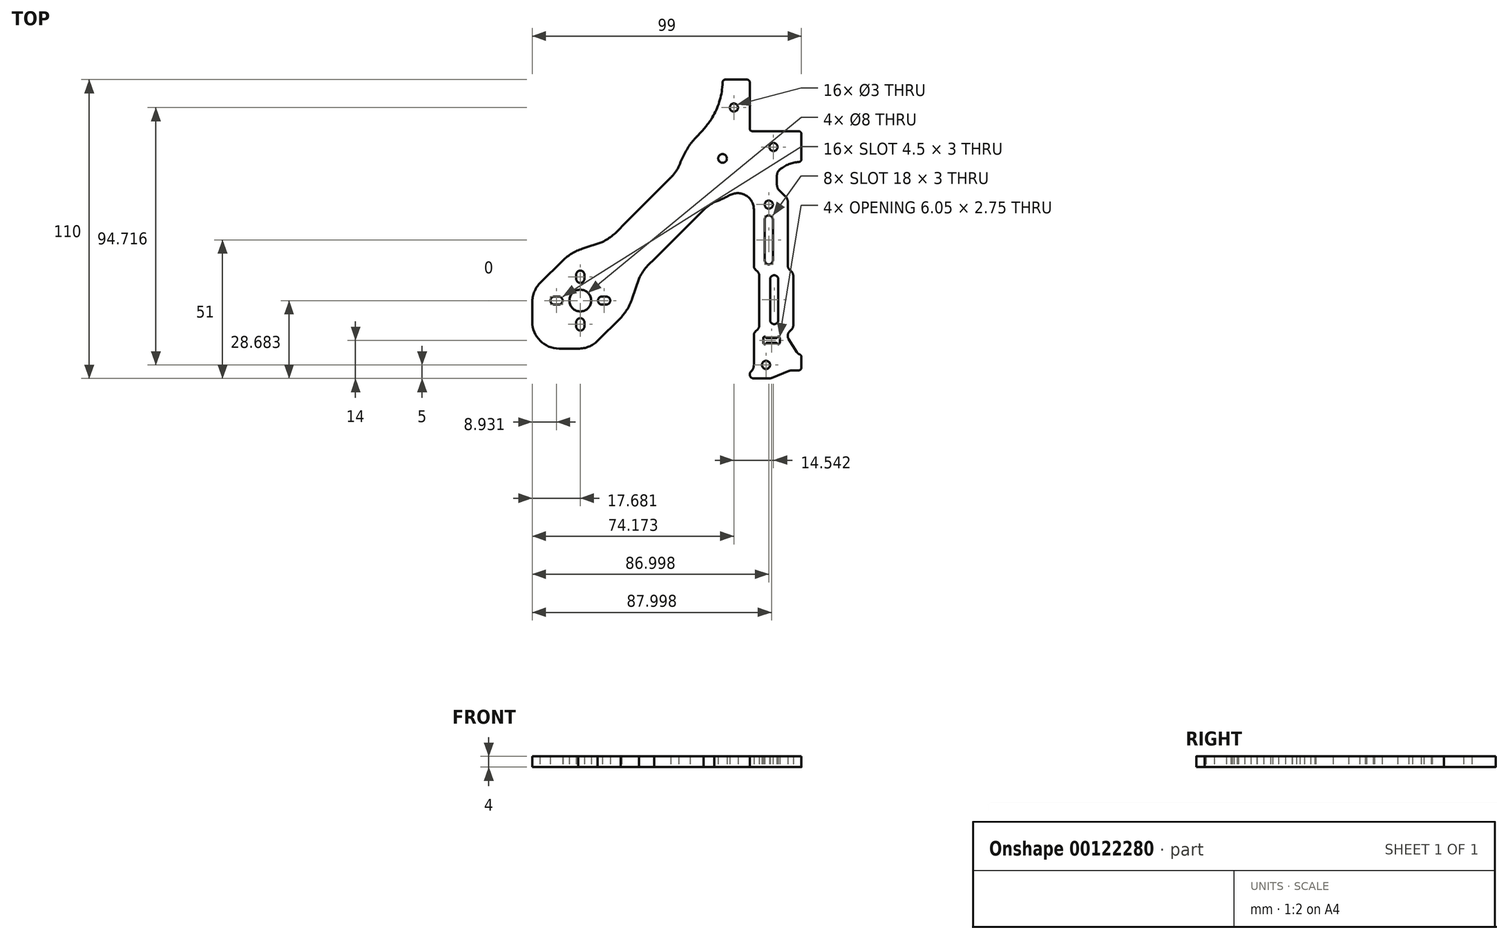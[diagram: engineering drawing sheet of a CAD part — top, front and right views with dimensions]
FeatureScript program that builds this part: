
annotation { "Feature Type Name" : "Feature", "Feature Type Description" : "" }
export const myFeature = defineFeature(function(context is Context, id is Id, definition is map)
    precondition{}
    {
        {
            var Q0;
            Q0=qCreatedBy(makeId("Top.planeOp"),FACE);
            var sketch = newSketch(context, id + "F0", { "sketchPlane" : qUnion([Q0])});
            skLineSegment(sketch, "E0", {"start": v(32, -55) * mm, "end": v(37.42, -55) * mm});
            skArc(sketch, "E1", {"start": v(31, -52.38) * mm, "mid": v(30.6, -54.04) * mm, "end": v(32, -55) * mm});
            skLineSegment(sketch, "E2", {"start": v(44.96, -52.21) * mm, "end": v(38.53, -54.79) * mm});
            skArc(sketch, "E3", {"start": v(31, -52.38) * mm, "mid": v(31.74, -51.37) * mm, "end": v(32, -50.15) * mm});
            skArc(sketch, "E4", {"start": v(37.42, -55) * mm, "mid": v(37.99, -54.95) * mm, "end": v(38.53, -54.79) * mm});
            skArc(sketch, "E5", {"start": v(46.08, -52) * mm, "mid": v(45.5, -52.05) * mm, "end": v(44.96, -52.21) * mm});
            skCircle(sketch, "E6", {"center": v(37.5, 9) * mm, "radius": 1.5 * mm});
            skLineSegment(sketch, "E7", {"start": v(46.08, -52) * mm, "end": v(48.5, -52) * mm});
            skArc(sketch, "E8", {"start": v(48.5, -52) * mm, "mid": v(49.2, -51.7) * mm, "end": v(49.5, -51) * mm});
            skLineSegment(sketch, "E9", {"start": v(33.41, -15.73) * mm, "end": v(32.58, -14.9) * mm});
            skLineSegment(sketch, "E10", {"start": v(32.58, -37.73) * mm, "end": v(33.41, -36.9) * mm});
            skLineSegment(sketch, "E11", {"start": v(32, -39.15) * mm, "end": v(32, -50.15) * mm});
            skLineSegment(sketch, "E12", {"start": v(34, -17.15) * mm, "end": v(34, -35.49) * mm});
            skArc(sketch, "E13", {"start": v(32.58, -37.73) * mm, "mid": v(32.15, -38.38) * mm, "end": v(32, -39.15) * mm});
            skArc(sketch, "E14", {"start": v(33.41, -36.9) * mm, "mid": v(33.85, -36.25) * mm, "end": v(34, -35.49) * mm});
            skArc(sketch, "E15", {"start": v(32, -13.49) * mm, "mid": v(32.15, -14.25) * mm, "end": v(32.58, -14.9) * mm});
            skArc(sketch, "E16", {"start": v(34, -17.15) * mm, "mid": v(33.85, -16.38) * mm, "end": v(33.41, -15.73) * mm});
            skCircle(sketch, "E17", {"center": v(-31.82, -26.32) * mm, "radius": 4 * mm});
            skArc(sketch, "E18", {"start": v(-41.32, -24.82) * mm, "mid": v(-42.82, -26.32) * mm, "end": v(-41.32, -27.82) * mm});
            skArc(sketch, "E19", {"start": v(-39.82, -27.82) * mm, "mid": v(-38.32, -26.32) * mm, "end": v(-39.82, -24.82) * mm});
            skArc(sketch, "E20", {"start": v(-30.32, -16.82) * mm, "mid": v(-31.82, -15.32) * mm, "end": v(-33.32, -16.82) * mm});
            skArc(sketch, "E21", {"start": v(-33.32, -18.32) * mm, "mid": v(-31.82, -19.82) * mm, "end": v(-30.32, -18.32) * mm});
            skArc(sketch, "E22", {"start": v(-23.82, -24.82) * mm, "mid": v(-25.32, -26.32) * mm, "end": v(-23.82, -27.82) * mm});
            skArc(sketch, "E23", {"start": v(-22.32, -27.82) * mm, "mid": v(-20.82, -26.32) * mm, "end": v(-22.32, -24.82) * mm});
            skArc(sketch, "E24", {"start": v(-30.32, -34.32) * mm, "mid": v(-31.82, -32.82) * mm, "end": v(-33.32, -34.32) * mm});
            skArc(sketch, "E25", {"start": v(-33.32, -35.82) * mm, "mid": v(-31.82, -37.32) * mm, "end": v(-30.32, -35.82) * mm});
            skLineSegment(sketch, "E26", {"start": v(-41.32, -24.82) * mm, "end": v(-39.82, -24.82) * mm});
            skLineSegment(sketch, "E27", {"start": v(-39.82, -27.82) * mm, "end": v(-41.32, -27.82) * mm});
            skLineSegment(sketch, "E28", {"start": v(-33.32, -16.82) * mm, "end": v(-33.32, -18.32) * mm});
            skLineSegment(sketch, "E29", {"start": v(-30.32, -16.82) * mm, "end": v(-30.32, -18.32) * mm});
            skLineSegment(sketch, "E30", {"start": v(-22.32, -24.82) * mm, "end": v(-23.82, -24.82) * mm});
            skLineSegment(sketch, "E31", {"start": v(-22.32, -27.82) * mm, "end": v(-23.82, -27.82) * mm});
            skLineSegment(sketch, "E32", {"start": v(-30.32, -34.32) * mm, "end": v(-30.32, -35.82) * mm});
            skLineSegment(sketch, "E33", {"start": v(-33.32, -34.32) * mm, "end": v(-33.32, -35.82) * mm});
            skLineSegment(sketch, "E34", {"start": v(-25.46, -41.17) * mm, "end": v(-16.97, -32.68) * mm});
            skLineSegment(sketch, "E35", {"start": v(-38.18, -11.47) * mm, "end": v(-46.67, -19.95) * mm});
            skArc(sketch, "E36", {"start": v(-49.5, -34.1) * mm, "mid": v(-46.6, -41.1) * mm, "end": v(-39.6, -44) * mm});
            skLineSegment(sketch, "E37", {"start": v(-49.5, -34.1) * mm, "end": v(-49.5, -27.02) * mm});
            skLineSegment(sketch, "E38", {"start": v(-39.6, -44) * mm, "end": v(-32.53, -44) * mm});
            skLineSegment(sketch, "E39", {"start": v(-12.73, -25.61) * mm, "end": v(-10.25, -18.19) * mm});
            skLineSegment(sketch, "E40", {"start": v(-31.11, -7.23) * mm, "end": v(-23.69, -4.75) * mm});
            skArc(sketch, "E41", {"start": v(-23.69, -4.75) * mm, "mid": v(-19.85, -2.3) * mm, "end": v(-16.62, 0.9) * mm});
            skArc(sketch, "E42", {"start": v(-4.6, -11.11) * mm, "mid": v(-7.8, -14.35) * mm, "end": v(-10.25, -18.19) * mm});
            skArc(sketch, "E43", {"start": v(-16.97, -32.68) * mm, "mid": v(-14.48, -29.37) * mm, "end": v(-12.73, -25.61) * mm});
            skArc(sketch, "E44", {"start": v(-31.11, -7.23) * mm, "mid": v(-34.87, -8.98) * mm, "end": v(-38.18, -11.47) * mm});
            skArc(sketch, "E45", {"start": v(-46.67, -19.95) * mm, "mid": v(-48.79, -23.2) * mm, "end": v(-49.5, -27.02) * mm});
            skArc(sketch, "E46", {"start": v(-32.53, -44) * mm, "mid": v(-28.7, -43.28) * mm, "end": v(-25.46, -41.17) * mm});
            skLineSegment(sketch, "E47", {"start": v(1.41, 18.94) * mm, "end": v(-16.62, 0.9) * mm});
            skLineSegment(sketch, "E48", {"start": v(32, 7.22) * mm, "end": v(32, -13.49) * mm});
            skArc(sketch, "E49", {"start": v(17.5, 9.92) * mm, "mid": v(15.37, 8.64) * mm, "end": v(13.5, 7) * mm});
            skArc(sketch, "E50", {"start": v(1.41, 18.94) * mm, "mid": v(3.1, 20.84) * mm, "end": v(4.42, 23) * mm});
            skLineSegment(sketch, "E51", {"start": v(46.5, -17.15) * mm, "end": v(46.5, -35.49) * mm});
            skLineSegment(sketch, "E52", {"start": v(45.08, -37.73) * mm, "end": v(45.91, -36.9) * mm});
            skLineSegment(sketch, "E53", {"start": v(45.91, -15.73) * mm, "end": v(45.08, -14.9) * mm});
            skLineSegment(sketch, "E54", {"start": v(44.5, -13.49) * mm, "end": v(44.5, 9.96) * mm});
            skLineSegment(sketch, "E55", {"start": v(44.5, -39.43) * mm, "end": v(44.5, -39.15) * mm});
            skArc(sketch, "E56", {"start": v(44.5, -13.49) * mm, "mid": v(44.65, -14.25) * mm, "end": v(45.08, -14.9) * mm});
            skArc(sketch, "E57", {"start": v(46.5, -17.15) * mm, "mid": v(46.35, -16.38) * mm, "end": v(45.91, -15.73) * mm});
            skArc(sketch, "E58", {"start": v(45.08, -37.73) * mm, "mid": v(44.65, -38.38) * mm, "end": v(44.5, -39.15) * mm});
            skArc(sketch, "E59", {"start": v(45.91, -36.9) * mm, "mid": v(46.35, -36.25) * mm, "end": v(46.5, -35.49) * mm});
            skLineSegment(sketch, "E60", {"start": v(41, -33.5) * mm, "end": v(41, -18.5) * mm});
            skLineSegment(sketch, "E61", {"start": v(38, -18.5) * mm, "end": v(38, -33.5) * mm});
            skArc(sketch, "E62", {"start": v(38, -33.5) * mm, "mid": v(39.5, -35) * mm, "end": v(41, -33.5) * mm});
            skArc(sketch, "E63", {"start": v(41, -18.5) * mm, "mid": v(39.5, -17) * mm, "end": v(38, -18.5) * mm});
            skLineSegment(sketch, "E64", {"start": v(39, -11.5) * mm, "end": v(39, 3.5) * mm});
            skLineSegment(sketch, "E65", {"start": v(36, 3.5) * mm, "end": v(36, -11.5) * mm});
            skArc(sketch, "E66", {"start": v(36, -11.5) * mm, "mid": v(37.5, -13) * mm, "end": v(39, -11.5) * mm});
            skArc(sketch, "E67", {"start": v(39, 3.5) * mm, "mid": v(37.5, 5) * mm, "end": v(36, 3.5) * mm});
            skCircle(sketch, "E68", {"center": v(39.22, 30.17) * mm, "radius": 1.5 * mm});
            skCircle(sketch, "E69", {"center": v(24.67, 44.72) * mm, "radius": 1.5 * mm});
            skLineSegment(sketch, "E70", {"start": v(44.8, -40.49) * mm, "end": v(47.8, -45.29) * mm});
            skArc(sketch, "E71", {"start": v(44.5, -39.43) * mm, "mid": v(44.58, -39.98) * mm, "end": v(44.8, -40.49) * mm});
            skLineSegment(sketch, "E72", {"start": v(49.5, -47.05) * mm, "end": v(49.5, -51) * mm});
            skArc(sketch, "E73", {"start": v(47.8, -45.29) * mm, "mid": v(48.25, -45.79) * mm, "end": v(48.83, -46.11) * mm});
            skArc(sketch, "E74", {"start": v(49.5, -47.05) * mm, "mid": v(49.31, -46.48) * mm, "end": v(48.83, -46.11) * mm});
            skLineSegment(sketch, "E75", {"start": v(-4.6, -11.11) * mm, "end": v(13.5, 7) * mm});
            skArc(sketch, "E76", {"start": v(30.5, 37) * mm, "mid": v(30.8, 36.3) * mm, "end": v(31.5, 36) * mm});
            skLineSegment(sketch, "E77", {"start": v(31.5, 36) * mm, "end": v(48.5, 36) * mm});
            skArc(sketch, "E78", {"start": v(49.5, 35) * mm, "mid": v(49.2, 35.7) * mm, "end": v(48.5, 36) * mm});
            skLineSegment(sketch, "E79", {"start": v(30.5, 54) * mm, "end": v(30.5, 37) * mm});
            skArc(sketch, "E80", {"start": v(30.5, 54) * mm, "mid": v(30.2, 54.7) * mm, "end": v(29.5, 55) * mm});
            skCircle(sketch, "E81", {"center": v(36.5, -50) * mm, "radius": 1.5 * mm});
            skCircle(sketch, "E82", {"center": v(20.5, 26) * mm, "radius": 1.6 * mm});
            skArc(sketch, "E83", {"start": v(16.27, 40.35) * mm, "mid": v(19.05, 46) * mm, "end": v(20.4, 52.17) * mm});
            skArc(sketch, "E84", {"start": v(11.73, 34.76) * mm, "mid": v(14.15, 37.44) * mm, "end": v(16.27, 40.35) * mm});
            skArc(sketch, "E85", {"start": v(11.73, 34.76) * mm, "mid": v(10.12, 33.04) * mm, "end": v(8.61, 31.23) * mm});
            skArc(sketch, "E86", {"start": v(8.61, 31.23) * mm, "mid": v(6.25, 27.25) * mm, "end": v(4.42, 23) * mm});
            skArc(sketch, "E87", {"start": v(17.5, 9.92) * mm, "mid": v(20.33, 11.06) * mm, "end": v(23.05, 12.45) * mm});
            skArc(sketch, "E88", {"start": v(20.4, 52.17) * mm, "mid": v(20.47, 53.1) * mm, "end": v(20.51, 54.03) * mm});
            skArc(sketch, "E89", {"start": v(21.51, 55) * mm, "mid": v(20.82, 54.72) * mm, "end": v(20.51, 54.03) * mm});
            skLineSegment(sketch, "E90", {"start": v(21.51, 55) * mm, "end": v(29.5, 55) * mm});
            skLineSegment(sketch, "E91", {"start": v(40.5, 19.66) * mm, "end": v(40.5, 16.3) * mm});
            skLineSegment(sketch, "E92", {"start": v(41.45, 14.11) * mm, "end": v(43.54, 12.16) * mm});
            skArc(sketch, "E93", {"start": v(48.57, 24.7) * mm, "mid": v(44.9, 23.87) * mm, "end": v(41.65, 22.02) * mm});
            skArc(sketch, "E94", {"start": v(48.57, 24.7) * mm, "mid": v(49.23, 25.01) * mm, "end": v(49.5, 25.7) * mm});
            skLineSegment(sketch, "E95", {"start": v(49.5, 35) * mm, "end": v(49.5, 25.7) * mm});
            skArc(sketch, "E96", {"start": v(44.5, 9.96) * mm, "mid": v(44.25, 11.16) * mm, "end": v(43.54, 12.16) * mm});
            skArc(sketch, "E97", {"start": v(40.5, 16.3) * mm, "mid": v(40.75, 15.1) * mm, "end": v(41.45, 14.11) * mm});
            skArc(sketch, "E98", {"start": v(41.65, 22.02) * mm, "mid": v(40.8, 20.97) * mm, "end": v(40.5, 19.66) * mm});
            skArc(sketch, "E99", {"start": v(32, 7.22) * mm, "mid": v(29.03, 12.4) * mm, "end": v(23.05, 12.45) * mm});
            skLineSegment(sketch, "E100", {"start": v(41.52, -41.88) * mm, "end": v(41.52, -40.12) * mm});
            skLineSegment(sketch, "E101", {"start": v(35.47, -40.12) * mm, "end": v(35.47, -41.88) * mm});
            skArc(sketch, "E102", {"start": v(36.4, -39.88) * mm, "mid": v(35.84, -39.64) * mm, "end": v(35.47, -40.12) * mm});
            skArc(sketch, "E103", {"start": v(35.47, -41.88) * mm, "mid": v(35.84, -42.36) * mm, "end": v(36.4, -42.12) * mm});
            skArc(sketch, "E104", {"start": v(40.59, -42.12) * mm, "mid": v(41.15, -42.36) * mm, "end": v(41.52, -41.88) * mm});
            skArc(sketch, "E105", {"start": v(41.52, -40.12) * mm, "mid": v(41.15, -39.64) * mm, "end": v(40.59, -39.88) * mm});
            skLineSegment(sketch, "E106", {"start": v(36.84, -40.12) * mm, "end": v(40.16, -40.12) * mm});
            skLineSegment(sketch, "E107", {"start": v(40.16, -41.88) * mm, "end": v(36.84, -41.88) * mm});
            skArc(sketch, "E108", {"start": v(36.4, -39.88) * mm, "mid": v(36.59, -40.06) * mm, "end": v(36.84, -40.12) * mm});
            skArc(sketch, "E109", {"start": v(40.16, -40.12) * mm, "mid": v(40.4, -40.06) * mm, "end": v(40.59, -39.88) * mm});
            skArc(sketch, "E110", {"start": v(40.59, -42.12) * mm, "mid": v(40.4, -41.94) * mm, "end": v(40.16, -41.88) * mm});
            skArc(sketch, "E111", {"start": v(36.84, -41.88) * mm, "mid": v(36.59, -41.94) * mm, "end": v(36.4, -42.12) * mm});
            skSolve(sketch);
        }
        {
            var Q0;
            Q0=qSketchRegion(id+"F0",true);
            extrude(context, id + "F1", {"entities" : qUnion([Q0]), "depth" : 4 * mm});
        }
    });
